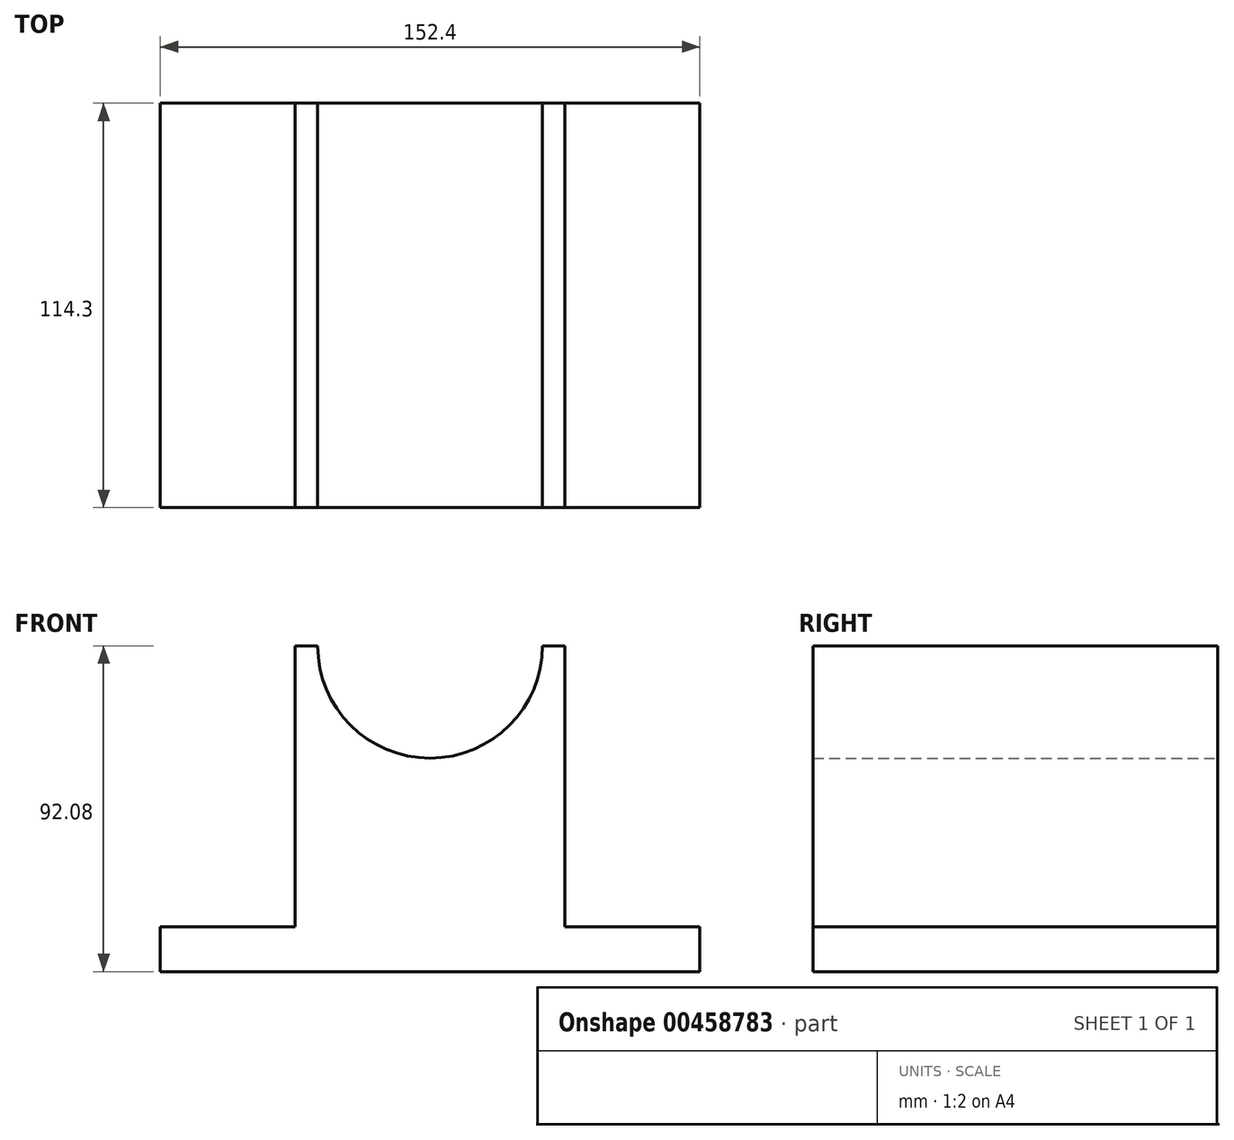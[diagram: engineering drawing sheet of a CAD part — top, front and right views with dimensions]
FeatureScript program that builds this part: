
annotation { "Feature Type Name" : "Feature", "Feature Type Description" : "" }
export const myFeature = defineFeature(function(context is Context, id is Id, definition is map)
    precondition{}
    {
        {
            var Q0;
            Q0=qCreatedBy(makeId("Front.planeOp"),FACE);
            var sketch = newSketch(context, id + "F0", { "sketchPlane" : qUnion([Q0])});
            skLineSegment(sketch, "E0", {"start": v(0, 0) * mm, "end": v(76.2, 0) * mm});
            skLineSegment(sketch, "E1", {"start": v(76.2, 0) * mm, "end": v(76.2, 12.7) * mm});
            skLineSegment(sketch, "E2", {"start": v(76.2, 12.7) * mm, "end": v(38.1, 12.7) * mm});
            skLineSegment(sketch, "E3", {"start": v(38.1, 12.7) * mm, "end": v(38.1, 92.07) * mm});
            skLineSegment(sketch, "E4", {"start": v(38.1, 92.07) * mm, "end": v(0, 92.07) * mm});
            skLineSegment(sketch, "E5", {"start": v(0, 92.07) * mm, "end": v(0, 0) * mm, "construction": true});
            skLineSegment(sketch, "E6.MirrorCS", {"start": v(-38.1, 92.07) * mm, "end": v(0, 92.07) * mm});
            skLineSegment(sketch, "E7.MirrorCS", {"start": v(-38.1, 12.7) * mm, "end": v(-38.1, 92.07) * mm});
            skLineSegment(sketch, "E8.MirrorCS", {"start": v(-76.2, 12.7) * mm, "end": v(-38.1, 12.7) * mm});
            skLineSegment(sketch, "E9.MirrorCS", {"start": v(-76.2, 0) * mm, "end": v(-76.2, 12.7) * mm});
            skLineSegment(sketch, "E10.MirrorCS", {"start": v(0, 0) * mm, "end": v(-76.2, 0) * mm});
            skArc(sketch, "E11", {"start": v(31.75, 92.07) * mm, "mid": v(0, 60.32) * mm, "end": v(-31.75, 92.07) * mm});
            skSolve(sketch);
        }
        {
            var Q0;
            Q0=makeQuery(id+"F0.imprint","IMPRINT",FACE,{"disambiguationData":[TD([[makeQuery(id+"F0.imprint","IMPRINT",EDGE,{"derivedFrom":sQuery(id+"F0.wireOp",EDGE,"E0")}),1.0]])]});
            extrude(context, id + "F1", {"entities" : qUnion([Q0]), "depth" : 114.3 * mm});
        }
    });
